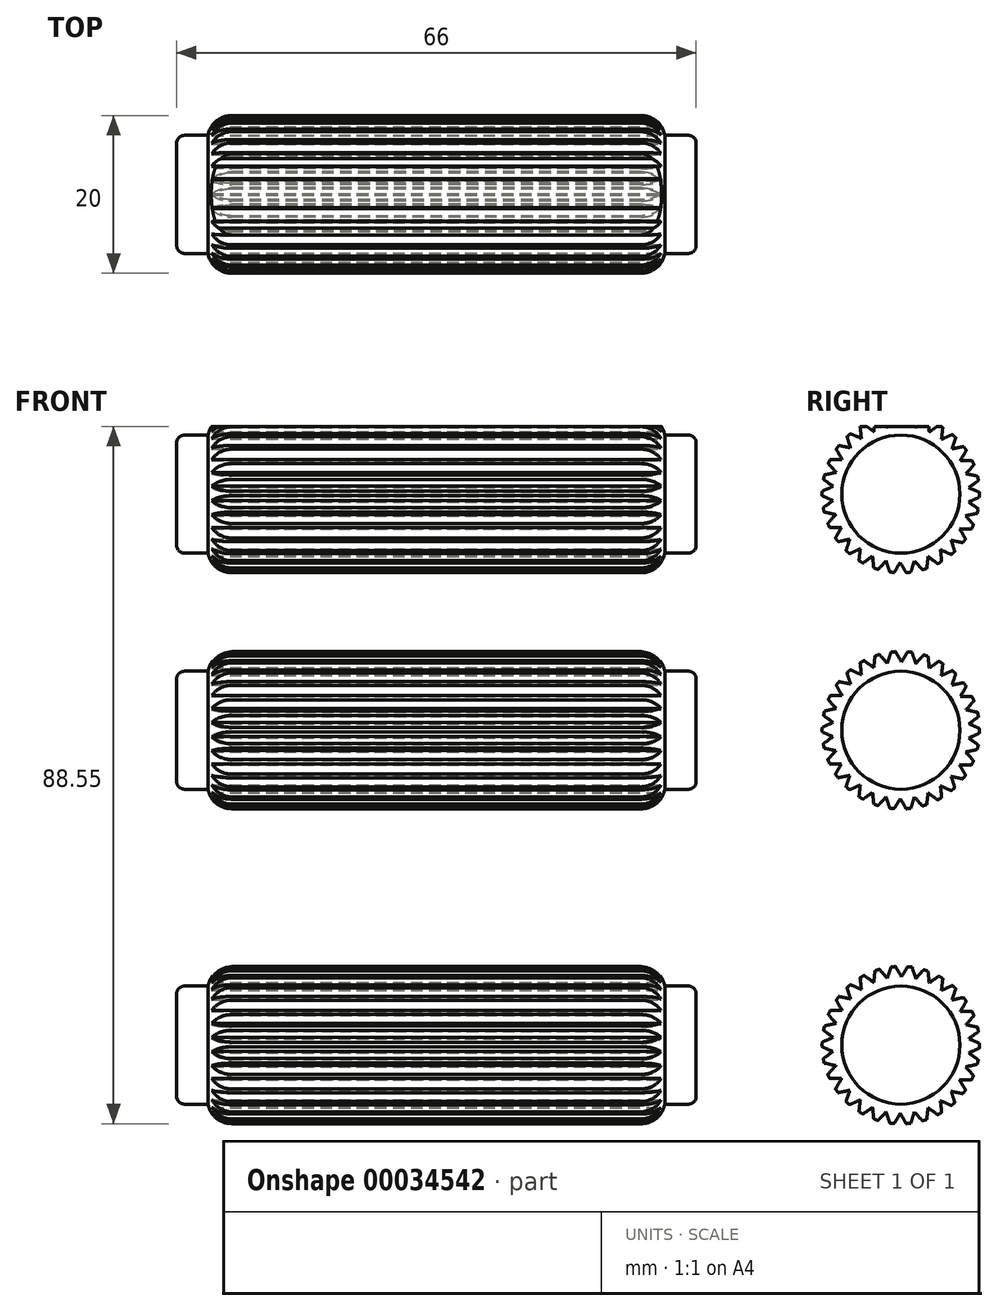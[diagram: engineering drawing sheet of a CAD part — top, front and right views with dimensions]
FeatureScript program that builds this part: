
annotation { "Feature Type Name" : "Feature", "Feature Type Description" : "" }
export const myFeature = defineFeature(function(context is Context, id is Id, definition is map)
    precondition{}
    {
        {
            var Q0;
            Q0=qCreatedBy(makeId("Top.planeOp"),FACE);
            var sketch = newSketch(context, id + "F0", { "sketchPlane" : qUnion([Q0])});
            skLineSegment(sketch, "E0.bottom", {"start": v(-73.95, 30.98) * mm, "end": v(-15.95, 30.98) * mm});
            skLineSegment(sketch, "E0.top", {"start": v(-73.95, 20.98) * mm, "end": v(-15.95, 20.98) * mm});
            skLineSegment(sketch, "E0.left", {"start": v(-73.95, 30.98) * mm, "end": v(-73.95, 20.98) * mm});
            skLineSegment(sketch, "E0.right", {"start": v(-15.95, 30.98) * mm, "end": v(-15.95, 20.98) * mm});
            skLineSegment(sketch, "E1.bottom", {"start": v(-15.95, 20.98) * mm, "end": v(-11.95, 20.98) * mm});
            skLineSegment(sketch, "E1.top", {"start": v(-15.95, 28.48) * mm, "end": v(-11.95, 28.48) * mm});
            skLineSegment(sketch, "E1.left", {"start": v(-15.95, 20.98) * mm, "end": v(-15.95, 28.48) * mm});
            skLineSegment(sketch, "E1.right", {"start": v(-11.95, 20.98) * mm, "end": v(-11.95, 28.48) * mm});
            skLineSegment(sketch, "E2", {"start": v(-44.95, 6.9) * mm, "end": v(-44.95, 44.2) * mm});
            skPoint(sketch, "E2.startSnap0", {"position": v(-44.95, 20.98) * mm});
            skLineSegment(sketch, "E3.MirrorCS", {"start": v(-73.95, 20.98) * mm, "end": v(-77.95, 20.98) * mm});
            skLineSegment(sketch, "E4.MirrorCS", {"start": v(-73.95, 20.98) * mm, "end": v(-73.95, 28.48) * mm});
            skLineSegment(sketch, "E5.MirrorCS", {"start": v(-77.95, 20.98) * mm, "end": v(-77.95, 28.48) * mm});
            skLineSegment(sketch, "E6.MirrorCS", {"start": v(-73.95, 28.48) * mm, "end": v(-77.95, 28.48) * mm});
            skSolve(sketch);
        }
        {
            var Q0;
            Q0=makeQuery(id+"F0.imprint","IMPRINT",FACE,{"disambiguationData":[TD([[makeQuery(id+"F0.imprint","IMPRINT",EDGE,{"derivedFrom":sQuery(id+"F0.wireOp",EDGE,"E3.MirrorCS")}),-1.0]])]});
            var Q1;
            {var subQ6=sQuery(id+"F0.wireOp",EDGE,"E0.left");Q1=makeQuery(id+"F0.imprint","IMPRINT",FACE,{"disambiguationData":[TD([[makeQuery(id+"F0.imprint","IMPRINT",EDGE,{"derivedFrom":subQ6}),1.0]])]});}
            var Q2;
            {var subQ6=sQuery(id+"F0.wireOp",EDGE,"E0.right");Q2=makeQuery(id+"F0.imprint","IMPRINT",FACE,{"disambiguationData":[TD([[makeQuery(id+"F0.imprint","IMPRINT",EDGE,{"derivedFrom":subQ6}),-1.0]])]});}
            var Q3;
            Q3=makeQuery(id+"F0.imprint","IMPRINT",FACE,{"disambiguationData":[TD([[makeQuery(id+"F0.imprint","IMPRINT",EDGE,{"derivedFrom":sQuery(id+"F0.wireOp",EDGE,"E1.bottom")}),1.0]])]});
            var Q4;
            Q4=sQuery(id+"F0.wireOp",EDGE,"E0.top");
            revolve(context, id + "F1", {"entities" : qUnion([Q0, Q1, Q2, Q3]), "axis" : qUnion([Q4]), "revolveType" : RevolveType.FULL});
        }
        {
            var Q0;
            Q0=qCreatedBy(makeId("Right.planeOp"),FACE);
            var sketch = newSketch(context, id + "F2", { "sketchPlane" : qUnion([Q0])});
            skCircle(sketch, "E7.0.0", {"center": v(20.98, 0) * mm, "radius": 7.5 * mm});
            skCircle(sketch, "E8.cCircle", {"center": v(21.07, 10) * mm, "radius": 0.66 * mm, "construction": true});
            skLineSegment(sketch, "E8.0", {"start": v(22.22, 10.65) * mm, "end": v(21.07, 8.67) * mm});
            skLineSegment(sketch, "E8.1", {"start": v(21.07, 8.67) * mm, "end": v(19.92, 10.65) * mm});
            skLineSegment(sketch, "E8.2", {"start": v(19.92, 10.65) * mm, "end": v(22.22, 10.65) * mm});
            skPoint(sketch, "E8.0.midPoint", {"position": v(21.64, 9.66) * mm});
            skLineSegment(sketch, "E9.1.0", {"start": v(19.27, 8.5) * mm, "end": v(17.73, 10.2) * mm});
            skLineSegment(sketch, "E9.1.1", {"start": v(19.98, 10.68) * mm, "end": v(19.27, 8.5) * mm});
            skLineSegment(sketch, "E9.1.2", {"start": v(17.73, 10.2) * mm, "end": v(19.98, 10.68) * mm});
            skLineSegment(sketch, "E9.2.0", {"start": v(17.54, 7.95) * mm, "end": v(15.68, 9.3) * mm});
            skLineSegment(sketch, "E9.2.1", {"start": v(17.78, 10.24) * mm, "end": v(17.54, 7.95) * mm});
            skLineSegment(sketch, "E9.2.2", {"start": v(15.68, 9.3) * mm, "end": v(17.78, 10.24) * mm});
            skLineSegment(sketch, "E10.1.3.0", {"start": v(15.96, 7.06) * mm, "end": v(13.86, 8) * mm});
            skLineSegment(sketch, "E10.3.3.0", {"start": v(15.72, 9.35) * mm, "end": v(15.96, 7.06) * mm});
            skLineSegment(sketch, "E10.6.3.0", {"start": v(13.86, 8) * mm, "end": v(15.72, 9.35) * mm});
            skLineSegment(sketch, "E10.1.4.0", {"start": v(14.6, 5.86) * mm, "end": v(12.35, 6.34) * mm});
            skLineSegment(sketch, "E10.3.4.0", {"start": v(13.9, 8.05) * mm, "end": v(14.6, 5.86) * mm});
            skLineSegment(sketch, "E10.6.4.0", {"start": v(12.35, 6.34) * mm, "end": v(13.9, 8.05) * mm});
            skLineSegment(sketch, "E10.1.5.0", {"start": v(13.52, 4.4) * mm, "end": v(11.23, 4.4) * mm});
            skLineSegment(sketch, "E10.3.5.0", {"start": v(12.37, 6.4) * mm, "end": v(13.52, 4.4) * mm});
            skLineSegment(sketch, "E10.6.5.0", {"start": v(11.23, 4.4) * mm, "end": v(12.37, 6.4) * mm});
            skLineSegment(sketch, "E10.1.6.0", {"start": v(12.77, 2.76) * mm, "end": v(10.52, 2.28) * mm});
            skLineSegment(sketch, "E10.3.6.0", {"start": v(11.23, 4.47) * mm, "end": v(12.77, 2.76) * mm});
            skLineSegment(sketch, "E10.6.6.0", {"start": v(10.52, 2.28) * mm, "end": v(11.23, 4.47) * mm});
            skLineSegment(sketch, "E10.1.7.0", {"start": v(12.37, 1) * mm, "end": v(10.28, 0.06) * mm});
            skLineSegment(sketch, "E10.3.7.0", {"start": v(10.52, 2.34) * mm, "end": v(12.37, 1) * mm});
            skLineSegment(sketch, "E10.6.7.0", {"start": v(10.28, 0.06) * mm, "end": v(10.52, 2.34) * mm});
            skLineSegment(sketch, "E10.1.8.0", {"start": v(12.36, -0.82) * mm, "end": v(10.5, -2.17) * mm});
            skLineSegment(sketch, "E10.3.8.0", {"start": v(10.26, 0.11) * mm, "end": v(12.36, -0.82) * mm});
            skLineSegment(sketch, "E10.6.8.0", {"start": v(10.5, -2.17) * mm, "end": v(10.26, 0.11) * mm});
            skLineSegment(sketch, "E10.1.9.0", {"start": v(12.71, -2.6) * mm, "end": v(11.18, -4.3) * mm});
            skLineSegment(sketch, "E10.3.9.0", {"start": v(10.47, -2.12) * mm, "end": v(12.71, -2.6) * mm});
            skLineSegment(sketch, "E10.6.9.0", {"start": v(11.18, -4.3) * mm, "end": v(10.47, -2.12) * mm});
            skLineSegment(sketch, "E10.1.10.0", {"start": v(13.43, -4.26) * mm, "end": v(12.29, -6.25) * mm});
            skLineSegment(sketch, "E10.3.10.0", {"start": v(11.14, -4.26) * mm, "end": v(13.43, -4.26) * mm});
            skLineSegment(sketch, "E10.6.10.0", {"start": v(12.29, -6.25) * mm, "end": v(11.14, -4.26) * mm});
            skLineSegment(sketch, "E10.1.11.0", {"start": v(14.48, -5.73) * mm, "end": v(13.78, -7.92) * mm});
            skLineSegment(sketch, "E10.3.11.0", {"start": v(12.24, -6.21) * mm, "end": v(14.48, -5.73) * mm});
            skLineSegment(sketch, "E10.6.11.0", {"start": v(13.78, -7.92) * mm, "end": v(12.24, -6.21) * mm});
            skLineSegment(sketch, "E10.1.12.0", {"start": v(15.82, -6.96) * mm, "end": v(15.58, -9.24) * mm});
            skLineSegment(sketch, "E10.3.12.0", {"start": v(13.72, -7.9) * mm, "end": v(15.82, -6.96) * mm});
            skLineSegment(sketch, "E10.6.12.0", {"start": v(15.58, -9.24) * mm, "end": v(13.72, -7.9) * mm});
            skLineSegment(sketch, "E10.1.13.0", {"start": v(17.38, -7.88) * mm, "end": v(17.62, -10.16) * mm});
            skLineSegment(sketch, "E10.3.13.0", {"start": v(15.52, -9.23) * mm, "end": v(17.38, -7.88) * mm});
            skLineSegment(sketch, "E10.6.13.0", {"start": v(17.62, -10.16) * mm, "end": v(15.52, -9.23) * mm});
            skLineSegment(sketch, "E10.1.14.0", {"start": v(19.1, -8.46) * mm, "end": v(19.8, -10.64) * mm});
            skLineSegment(sketch, "E10.3.14.0", {"start": v(17.56, -10.16) * mm, "end": v(19.1, -8.46) * mm});
            skLineSegment(sketch, "E10.6.14.0", {"start": v(19.8, -10.64) * mm, "end": v(17.56, -10.16) * mm});
            skLineSegment(sketch, "E10.1.15.0", {"start": v(20.9, -8.67) * mm, "end": v(22.04, -10.65) * mm});
            skLineSegment(sketch, "E10.3.15.0", {"start": v(19.75, -10.65) * mm, "end": v(20.9, -8.67) * mm});
            skLineSegment(sketch, "E10.6.15.0", {"start": v(22.04, -10.65) * mm, "end": v(19.75, -10.65) * mm});
            skLineSegment(sketch, "E10.1.16.0", {"start": v(22.7, -8.5) * mm, "end": v(24.24, -10.2) * mm});
            skLineSegment(sketch, "E10.3.16.0", {"start": v(22, -10.68) * mm, "end": v(22.7, -8.5) * mm});
            skLineSegment(sketch, "E10.6.16.0", {"start": v(24.24, -10.2) * mm, "end": v(22, -10.68) * mm});
            skLineSegment(sketch, "E10.1.17.0", {"start": v(24.43, -7.95) * mm, "end": v(26.29, -9.3) * mm});
            skLineSegment(sketch, "E10.3.17.0", {"start": v(24.19, -10.24) * mm, "end": v(24.43, -7.95) * mm});
            skLineSegment(sketch, "E10.6.17.0", {"start": v(26.29, -9.3) * mm, "end": v(24.19, -10.24) * mm});
            skLineSegment(sketch, "E10.1.18.0", {"start": v(26, -7.06) * mm, "end": v(28.1, -8) * mm});
            skLineSegment(sketch, "E10.3.18.0", {"start": v(26.25, -9.35) * mm, "end": v(26, -7.06) * mm});
            skLineSegment(sketch, "E10.6.18.0", {"start": v(28.1, -8) * mm, "end": v(26.25, -9.35) * mm});
            skLineSegment(sketch, "E10.1.19.0", {"start": v(27.36, -5.86) * mm, "end": v(29.61, -6.34) * mm});
            skLineSegment(sketch, "E10.3.19.0", {"start": v(28.07, -8.05) * mm, "end": v(27.36, -5.86) * mm});
            skLineSegment(sketch, "E10.6.19.0", {"start": v(29.61, -6.34) * mm, "end": v(28.07, -8.05) * mm});
            skLineSegment(sketch, "E11.1.20.0", {"start": v(28.44, -4.4) * mm, "end": v(30.74, -4.4) * mm});
            skLineSegment(sketch, "E11.3.20.0", {"start": v(29.6, -6.4) * mm, "end": v(28.44, -4.4) * mm});
            skLineSegment(sketch, "E11.6.20.0", {"start": v(30.74, -4.4) * mm, "end": v(29.6, -6.4) * mm});
            skLineSegment(sketch, "E11.1.21.0", {"start": v(29.2, -2.76) * mm, "end": v(31.44, -2.28) * mm});
            skLineSegment(sketch, "E11.3.21.0", {"start": v(30.73, -4.47) * mm, "end": v(29.2, -2.76) * mm});
            skLineSegment(sketch, "E11.6.21.0", {"start": v(31.44, -2.28) * mm, "end": v(30.73, -4.47) * mm});
            skLineSegment(sketch, "E11.1.22.0", {"start": v(29.6, -1) * mm, "end": v(31.69, -0.06) * mm});
            skLineSegment(sketch, "E11.3.22.0", {"start": v(31.45, -2.34) * mm, "end": v(29.6, -1) * mm});
            skLineSegment(sketch, "E11.6.22.0", {"start": v(31.69, -0.06) * mm, "end": v(31.45, -2.34) * mm});
            skLineSegment(sketch, "E11.1.23.0", {"start": v(29.61, 0.82) * mm, "end": v(31.47, 2.17) * mm});
            skLineSegment(sketch, "E11.3.23.0", {"start": v(31.7, -0.11) * mm, "end": v(29.61, 0.82) * mm});
            skLineSegment(sketch, "E11.6.23.0", {"start": v(31.47, 2.17) * mm, "end": v(31.7, -0.11) * mm});
            skLineSegment(sketch, "E11.1.24.0", {"start": v(29.25, 2.6) * mm, "end": v(30.79, 4.3) * mm});
            skLineSegment(sketch, "E11.3.24.0", {"start": v(31.5, 2.12) * mm, "end": v(29.25, 2.6) * mm});
            skLineSegment(sketch, "E11.6.24.0", {"start": v(30.79, 4.3) * mm, "end": v(31.5, 2.12) * mm});
            skLineSegment(sketch, "E11.1.25.0", {"start": v(28.53, 4.26) * mm, "end": v(29.68, 6.25) * mm});
            skLineSegment(sketch, "E11.3.25.0", {"start": v(30.83, 4.26) * mm, "end": v(28.53, 4.26) * mm});
            skLineSegment(sketch, "E11.6.25.0", {"start": v(29.68, 6.25) * mm, "end": v(30.83, 4.26) * mm});
            skLineSegment(sketch, "E11.1.26.0", {"start": v(27.48, 5.73) * mm, "end": v(28.2, 7.92) * mm});
            skLineSegment(sketch, "E11.3.26.0", {"start": v(29.73, 6.21) * mm, "end": v(27.48, 5.73) * mm});
            skLineSegment(sketch, "E11.6.26.0", {"start": v(28.2, 7.92) * mm, "end": v(29.73, 6.21) * mm});
            skLineSegment(sketch, "E11.1.27.0", {"start": v(26.15, 6.96) * mm, "end": v(26.39, 9.24) * mm});
            skLineSegment(sketch, "E11.3.27.0", {"start": v(28.24, 7.9) * mm, "end": v(26.15, 6.96) * mm});
            skLineSegment(sketch, "E11.6.27.0", {"start": v(26.39, 9.24) * mm, "end": v(28.24, 7.9) * mm});
            skLineSegment(sketch, "E11.1.28.0", {"start": v(24.59, 7.88) * mm, "end": v(24.35, 10.16) * mm});
            skLineSegment(sketch, "E11.3.28.0", {"start": v(26.44, 9.23) * mm, "end": v(24.59, 7.88) * mm});
            skLineSegment(sketch, "E11.6.28.0", {"start": v(24.35, 10.16) * mm, "end": v(26.44, 9.23) * mm});
            skLineSegment(sketch, "E11.1.29.0", {"start": v(22.87, 8.46) * mm, "end": v(22.16, 10.64) * mm});
            skLineSegment(sketch, "E11.3.29.0", {"start": v(24.4, 10.16) * mm, "end": v(22.87, 8.46) * mm});
            skLineSegment(sketch, "E11.6.29.0", {"start": v(22.16, 10.64) * mm, "end": v(24.4, 10.16) * mm});
            skSolve(sketch);
        }
        {
            var Q0;
            {var subQ0=sQuery(id+"F0.wireOp",EDGE,"E0.bottom");var subQ1=sQuery(id+"F0.wireOp",EDGE,"E0.right");var subQ3=sQuery(id+"F2.wireOp",EDGE,"E9.2.0");Q0=makeQuery(id+"F5.boolean.opBoolean","SPLIT",EDGE,{"disambiguationData":[TD([makeQuery(id+"F5.opExtrude","SWEPT_FACE",FACE,{"disambiguationData":[OSD([subQ3]),TDD([makeQuery(id+"F2.imprint","IMPRINT",EDGE,{"disambiguationData":[TD([[makeQuery(id+"F2.imprint","INTERSECT",VERTEX,{"derivedFrom":[subQ3,sQuery(id+"F2.wireOp",EDGE,"E9.2.1")]}),-1.0]])],"derivedFrom":subQ3})])]})])],"derivedFrom":makeQuery(id+"F1.opRevolve","SWEPT_EDGE",EDGE,{"disambiguationData":[OSD([subQ0,subQ1])]})});}
            var Q1;
            {var subQ0=sQuery(id+"F0.wireOp",EDGE,"E0.bottom");var subQ1=sQuery(id+"F0.wireOp",EDGE,"E0.right");var subQ3=sQuery(id+"F2.wireOp",EDGE,"E10.1.3.0");Q1=makeQuery(id+"F5.boolean.opBoolean","SPLIT",EDGE,{"disambiguationData":[TD([makeQuery(id+"F5.opExtrude","SWEPT_FACE",FACE,{"disambiguationData":[OSD([subQ3]),TDD([makeQuery(id+"F2.imprint","IMPRINT",EDGE,{"disambiguationData":[TD([[makeQuery(id+"F2.imprint","INTERSECT",VERTEX,{"derivedFrom":[subQ3,sQuery(id+"F2.wireOp",EDGE,"E10.3.3.0")]}),-1.0]])],"derivedFrom":subQ3})])]})])],"derivedFrom":makeQuery(id+"F1.opRevolve","SWEPT_EDGE",EDGE,{"disambiguationData":[OSD([subQ0,subQ1])]})});}
            fillet(context, id + "F3", {"entities" : qUnion([Q0, Q1]), "radius" : 3 * mm, "tangentPropagation" : true, "allowEdgeOverflow" : false});
        }
        {
            var Q0;
            Q0=makeQuery(id+"F1.opRevolve","SWEPT_EDGE",EDGE,{"disambiguationData":[OSD([sQuery(id+"F0.wireOp",EDGE,"E0.bottom"),sQuery(id+"F0.wireOp",EDGE,"E0.left")])]});
            fillet(context, id + "F4", {"entities" : qUnion([Q0]), "radius" : 3 * mm, "tangentPropagation" : true, "allowEdgeOverflow" : false});
        }
        {
            var Q0;
            {var subQ7=sQuery(id+"F2.wireOp",EDGE,"E9.1.0");var subQ10=sQuery(id+"F2.wireOp",EDGE,"E9.1.2");var subQ12=makeQuery(id+"F2.imprint","INTERSECT",VERTEX,{"derivedFrom":[subQ7,subQ10]});Q0=makeQuery(id+"F2.imprint","IMPRINT",FACE,{"disambiguationData":[TD([[makeQuery(id+"F2.imprint","IMPRINT",EDGE,{"disambiguationData":[TD([[subQ12,1.0]])],"derivedFrom":subQ7}),1.0]])]});}
            var Q1;
            {var subQ7=sQuery(id+"F2.wireOp",EDGE,"E8.1");var subQ10=sQuery(id+"F2.wireOp",EDGE,"E8.2");var subQ12=makeQuery(id+"F2.imprint","INTERSECT",VERTEX,{"derivedFrom":[subQ7,subQ10]});Q1=makeQuery(id+"F2.imprint","IMPRINT",FACE,{"disambiguationData":[TD([[makeQuery(id+"F2.imprint","IMPRINT",EDGE,{"disambiguationData":[TD([[subQ12,1.0]])],"derivedFrom":subQ7}),1.0]])]});}
            var Q2;
            {var subQ7=sQuery(id+"F2.wireOp",EDGE,"E9.2.0");var subQ10=sQuery(id+"F2.wireOp",EDGE,"E9.2.2");var subQ12=makeQuery(id+"F2.imprint","INTERSECT",VERTEX,{"derivedFrom":[subQ7,subQ10]});Q2=makeQuery(id+"F2.imprint","IMPRINT",FACE,{"disambiguationData":[TD([[makeQuery(id+"F2.imprint","IMPRINT",EDGE,{"disambiguationData":[TD([[subQ12,1.0]])],"derivedFrom":subQ7}),1.0]])]});}
            var Q3;
            {var subQ7=sQuery(id+"F2.wireOp",EDGE,"E10.1.3.0");var subQ10=sQuery(id+"F2.wireOp",EDGE,"E10.6.3.0");var subQ12=makeQuery(id+"F2.imprint","INTERSECT",VERTEX,{"derivedFrom":[subQ7,subQ10]});Q3=makeQuery(id+"F2.imprint","IMPRINT",FACE,{"disambiguationData":[TD([[makeQuery(id+"F2.imprint","IMPRINT",EDGE,{"disambiguationData":[TD([[subQ12,1.0]])],"derivedFrom":subQ7}),1.0]])]});}
            var Q4;
            {var subQ7=sQuery(id+"F2.wireOp",EDGE,"E10.1.4.0");var subQ10=sQuery(id+"F2.wireOp",EDGE,"E10.6.4.0");var subQ12=makeQuery(id+"F2.imprint","INTERSECT",VERTEX,{"derivedFrom":[subQ7,subQ10]});Q4=makeQuery(id+"F2.imprint","IMPRINT",FACE,{"disambiguationData":[TD([[makeQuery(id+"F2.imprint","IMPRINT",EDGE,{"disambiguationData":[TD([[subQ12,1.0]])],"derivedFrom":subQ7}),1.0]])]});}
            var Q5;
            {var subQ7=sQuery(id+"F2.wireOp",EDGE,"E10.1.5.0");var subQ10=sQuery(id+"F2.wireOp",EDGE,"E10.6.5.0");var subQ12=makeQuery(id+"F2.imprint","INTERSECT",VERTEX,{"derivedFrom":[subQ7,subQ10]});Q5=makeQuery(id+"F2.imprint","IMPRINT",FACE,{"disambiguationData":[TD([[makeQuery(id+"F2.imprint","IMPRINT",EDGE,{"disambiguationData":[TD([[subQ12,1.0]])],"derivedFrom":subQ7}),1.0]])]});}
            var Q6;
            {var subQ7=sQuery(id+"F2.wireOp",EDGE,"E10.1.6.0");var subQ10=sQuery(id+"F2.wireOp",EDGE,"E10.6.6.0");var subQ12=makeQuery(id+"F2.imprint","INTERSECT",VERTEX,{"derivedFrom":[subQ7,subQ10]});Q6=makeQuery(id+"F2.imprint","IMPRINT",FACE,{"disambiguationData":[TD([[makeQuery(id+"F2.imprint","IMPRINT",EDGE,{"disambiguationData":[TD([[subQ12,1.0]])],"derivedFrom":subQ7}),1.0]])]});}
            var Q7;
            {var subQ7=sQuery(id+"F2.wireOp",EDGE,"E10.1.8.0");var subQ10=sQuery(id+"F2.wireOp",EDGE,"E10.6.8.0");var subQ12=makeQuery(id+"F2.imprint","INTERSECT",VERTEX,{"derivedFrom":[subQ7,subQ10]});Q7=makeQuery(id+"F2.imprint","IMPRINT",FACE,{"disambiguationData":[TD([[makeQuery(id+"F2.imprint","IMPRINT",EDGE,{"disambiguationData":[TD([[subQ12,1.0]])],"derivedFrom":subQ7}),1.0]])]});}
            var Q8;
            {var subQ7=sQuery(id+"F2.wireOp",EDGE,"E10.1.7.0");var subQ10=sQuery(id+"F2.wireOp",EDGE,"E10.6.7.0");var subQ12=makeQuery(id+"F2.imprint","INTERSECT",VERTEX,{"derivedFrom":[subQ7,subQ10]});Q8=makeQuery(id+"F2.imprint","IMPRINT",FACE,{"disambiguationData":[TD([[makeQuery(id+"F2.imprint","IMPRINT",EDGE,{"disambiguationData":[TD([[subQ12,1.0]])],"derivedFrom":subQ7}),1.0]])]});}
            var Q9;
            {var subQ7=sQuery(id+"F2.wireOp",EDGE,"E10.1.9.0");var subQ10=sQuery(id+"F2.wireOp",EDGE,"E10.6.9.0");var subQ12=makeQuery(id+"F2.imprint","INTERSECT",VERTEX,{"derivedFrom":[subQ7,subQ10]});Q9=makeQuery(id+"F2.imprint","IMPRINT",FACE,{"disambiguationData":[TD([[makeQuery(id+"F2.imprint","IMPRINT",EDGE,{"disambiguationData":[TD([[subQ12,1.0]])],"derivedFrom":subQ7}),1.0]])]});}
            var Q10;
            {var subQ7=sQuery(id+"F2.wireOp",EDGE,"E10.1.10.0");var subQ10=sQuery(id+"F2.wireOp",EDGE,"E10.6.10.0");var subQ12=makeQuery(id+"F2.imprint","INTERSECT",VERTEX,{"derivedFrom":[subQ7,subQ10]});Q10=makeQuery(id+"F2.imprint","IMPRINT",FACE,{"disambiguationData":[TD([[makeQuery(id+"F2.imprint","IMPRINT",EDGE,{"disambiguationData":[TD([[subQ12,1.0]])],"derivedFrom":subQ7}),1.0]])]});}
            var Q11;
            {var subQ7=sQuery(id+"F2.wireOp",EDGE,"E10.1.11.0");var subQ10=sQuery(id+"F2.wireOp",EDGE,"E10.6.11.0");var subQ12=makeQuery(id+"F2.imprint","INTERSECT",VERTEX,{"derivedFrom":[subQ7,subQ10]});Q11=makeQuery(id+"F2.imprint","IMPRINT",FACE,{"disambiguationData":[TD([[makeQuery(id+"F2.imprint","IMPRINT",EDGE,{"disambiguationData":[TD([[subQ12,1.0]])],"derivedFrom":subQ7}),1.0]])]});}
            var Q12;
            {var subQ7=sQuery(id+"F2.wireOp",EDGE,"E10.1.13.0");var subQ10=sQuery(id+"F2.wireOp",EDGE,"E10.6.13.0");var subQ12=makeQuery(id+"F2.imprint","INTERSECT",VERTEX,{"derivedFrom":[subQ7,subQ10]});Q12=makeQuery(id+"F2.imprint","IMPRINT",FACE,{"disambiguationData":[TD([[makeQuery(id+"F2.imprint","IMPRINT",EDGE,{"disambiguationData":[TD([[subQ12,1.0]])],"derivedFrom":subQ7}),1.0]])]});}
            var Q13;
            {var subQ7=sQuery(id+"F2.wireOp",EDGE,"E10.1.14.0");var subQ10=sQuery(id+"F2.wireOp",EDGE,"E10.6.14.0");var subQ12=makeQuery(id+"F2.imprint","INTERSECT",VERTEX,{"derivedFrom":[subQ7,subQ10]});Q13=makeQuery(id+"F2.imprint","IMPRINT",FACE,{"disambiguationData":[TD([[makeQuery(id+"F2.imprint","IMPRINT",EDGE,{"disambiguationData":[TD([[subQ12,1.0]])],"derivedFrom":subQ7}),1.0]])]});}
            var Q14;
            {var subQ7=sQuery(id+"F2.wireOp",EDGE,"E10.1.15.0");var subQ10=sQuery(id+"F2.wireOp",EDGE,"E10.6.15.0");var subQ12=makeQuery(id+"F2.imprint","INTERSECT",VERTEX,{"derivedFrom":[subQ7,subQ10]});Q14=makeQuery(id+"F2.imprint","IMPRINT",FACE,{"disambiguationData":[TD([[makeQuery(id+"F2.imprint","IMPRINT",EDGE,{"disambiguationData":[TD([[subQ12,1.0]])],"derivedFrom":subQ7}),1.0]])]});}
            var Q15;
            {var subQ7=sQuery(id+"F2.wireOp",EDGE,"E10.1.16.0");var subQ10=sQuery(id+"F2.wireOp",EDGE,"E10.6.16.0");var subQ12=makeQuery(id+"F2.imprint","INTERSECT",VERTEX,{"derivedFrom":[subQ7,subQ10]});Q15=makeQuery(id+"F2.imprint","IMPRINT",FACE,{"disambiguationData":[TD([[makeQuery(id+"F2.imprint","IMPRINT",EDGE,{"disambiguationData":[TD([[subQ12,1.0]])],"derivedFrom":subQ7}),1.0]])]});}
            var Q16;
            {var subQ7=sQuery(id+"F2.wireOp",EDGE,"E10.1.17.0");var subQ10=sQuery(id+"F2.wireOp",EDGE,"E10.6.17.0");var subQ12=makeQuery(id+"F2.imprint","INTERSECT",VERTEX,{"derivedFrom":[subQ7,subQ10]});Q16=makeQuery(id+"F2.imprint","IMPRINT",FACE,{"disambiguationData":[TD([[makeQuery(id+"F2.imprint","IMPRINT",EDGE,{"disambiguationData":[TD([[subQ12,1.0]])],"derivedFrom":subQ7}),1.0]])]});}
            var Q17;
            {var subQ7=sQuery(id+"F2.wireOp",EDGE,"E10.1.18.0");var subQ10=sQuery(id+"F2.wireOp",EDGE,"E10.6.18.0");var subQ12=makeQuery(id+"F2.imprint","INTERSECT",VERTEX,{"derivedFrom":[subQ7,subQ10]});Q17=makeQuery(id+"F2.imprint","IMPRINT",FACE,{"disambiguationData":[TD([[makeQuery(id+"F2.imprint","IMPRINT",EDGE,{"disambiguationData":[TD([[subQ12,1.0]])],"derivedFrom":subQ7}),1.0]])]});}
            var Q18;
            {var subQ7=sQuery(id+"F2.wireOp",EDGE,"E10.1.19.0");var subQ10=sQuery(id+"F2.wireOp",EDGE,"E10.6.19.0");var subQ12=makeQuery(id+"F2.imprint","INTERSECT",VERTEX,{"derivedFrom":[subQ7,subQ10]});Q18=makeQuery(id+"F2.imprint","IMPRINT",FACE,{"disambiguationData":[TD([[makeQuery(id+"F2.imprint","IMPRINT",EDGE,{"disambiguationData":[TD([[subQ12,1.0]])],"derivedFrom":subQ7}),1.0]])]});}
            var Q19;
            {var subQ7=sQuery(id+"F2.wireOp",EDGE,"E11.1.20.0");var subQ10=sQuery(id+"F2.wireOp",EDGE,"E11.6.20.0");var subQ12=makeQuery(id+"F2.imprint","INTERSECT",VERTEX,{"derivedFrom":[subQ7,subQ10]});Q19=makeQuery(id+"F2.imprint","IMPRINT",FACE,{"disambiguationData":[TD([[makeQuery(id+"F2.imprint","IMPRINT",EDGE,{"disambiguationData":[TD([[subQ12,1.0]])],"derivedFrom":subQ7}),1.0]])]});}
            var Q20;
            {var subQ7=sQuery(id+"F2.wireOp",EDGE,"E11.1.21.0");var subQ10=sQuery(id+"F2.wireOp",EDGE,"E11.6.21.0");var subQ12=makeQuery(id+"F2.imprint","INTERSECT",VERTEX,{"derivedFrom":[subQ7,subQ10]});Q20=makeQuery(id+"F2.imprint","IMPRINT",FACE,{"disambiguationData":[TD([[makeQuery(id+"F2.imprint","IMPRINT",EDGE,{"disambiguationData":[TD([[subQ12,1.0]])],"derivedFrom":subQ7}),1.0]])]});}
            var Q21;
            {var subQ7=sQuery(id+"F2.wireOp",EDGE,"E11.1.22.0");var subQ10=sQuery(id+"F2.wireOp",EDGE,"E11.6.22.0");var subQ12=makeQuery(id+"F2.imprint","INTERSECT",VERTEX,{"derivedFrom":[subQ7,subQ10]});Q21=makeQuery(id+"F2.imprint","IMPRINT",FACE,{"disambiguationData":[TD([[makeQuery(id+"F2.imprint","IMPRINT",EDGE,{"disambiguationData":[TD([[subQ12,1.0]])],"derivedFrom":subQ7}),1.0]])]});}
            var Q22;
            {var subQ7=sQuery(id+"F2.wireOp",EDGE,"E11.1.23.0");var subQ10=sQuery(id+"F2.wireOp",EDGE,"E11.6.23.0");var subQ12=makeQuery(id+"F2.imprint","INTERSECT",VERTEX,{"derivedFrom":[subQ7,subQ10]});Q22=makeQuery(id+"F2.imprint","IMPRINT",FACE,{"disambiguationData":[TD([[makeQuery(id+"F2.imprint","IMPRINT",EDGE,{"disambiguationData":[TD([[subQ12,1.0]])],"derivedFrom":subQ7}),1.0]])]});}
            var Q23;
            {var subQ7=sQuery(id+"F2.wireOp",EDGE,"E11.1.24.0");var subQ10=sQuery(id+"F2.wireOp",EDGE,"E11.6.24.0");var subQ12=makeQuery(id+"F2.imprint","INTERSECT",VERTEX,{"derivedFrom":[subQ7,subQ10]});Q23=makeQuery(id+"F2.imprint","IMPRINT",FACE,{"disambiguationData":[TD([[makeQuery(id+"F2.imprint","IMPRINT",EDGE,{"disambiguationData":[TD([[subQ12,1.0]])],"derivedFrom":subQ7}),1.0]])]});}
            var Q24;
            {var subQ7=sQuery(id+"F2.wireOp",EDGE,"E11.1.25.0");var subQ10=sQuery(id+"F2.wireOp",EDGE,"E11.6.25.0");var subQ12=makeQuery(id+"F2.imprint","INTERSECT",VERTEX,{"derivedFrom":[subQ7,subQ10]});Q24=makeQuery(id+"F2.imprint","IMPRINT",FACE,{"disambiguationData":[TD([[makeQuery(id+"F2.imprint","IMPRINT",EDGE,{"disambiguationData":[TD([[subQ12,1.0]])],"derivedFrom":subQ7}),1.0]])]});}
            var Q25;
            {var subQ7=sQuery(id+"F2.wireOp",EDGE,"E11.1.26.0");var subQ10=sQuery(id+"F2.wireOp",EDGE,"E11.6.26.0");var subQ12=makeQuery(id+"F2.imprint","INTERSECT",VERTEX,{"derivedFrom":[subQ7,subQ10]});Q25=makeQuery(id+"F2.imprint","IMPRINT",FACE,{"disambiguationData":[TD([[makeQuery(id+"F2.imprint","IMPRINT",EDGE,{"disambiguationData":[TD([[subQ12,1.0]])],"derivedFrom":subQ7}),1.0]])]});}
            var Q26;
            {var subQ7=sQuery(id+"F2.wireOp",EDGE,"E11.1.27.0");var subQ10=sQuery(id+"F2.wireOp",EDGE,"E11.6.27.0");var subQ12=makeQuery(id+"F2.imprint","INTERSECT",VERTEX,{"derivedFrom":[subQ7,subQ10]});Q26=makeQuery(id+"F2.imprint","IMPRINT",FACE,{"disambiguationData":[TD([[makeQuery(id+"F2.imprint","IMPRINT",EDGE,{"disambiguationData":[TD([[subQ12,1.0]])],"derivedFrom":subQ7}),1.0]])]});}
            var Q27;
            {var subQ0=sQuery(id+"F2.wireOp",EDGE,"E11.6.29.0");var subQ1=sQuery(id+"F2.wireOp",EDGE,"E8.0");var subQ2=makeQuery(id+"F2.imprint","INTERSECT",VERTEX,{"derivedFrom":[subQ1,subQ0]});Q27=makeQuery(id+"F2.imprint","IMPRINT",FACE,{"disambiguationData":[TD([[makeQuery(id+"F2.imprint","IMPRINT",EDGE,{"disambiguationData":[TD([[subQ2,-1.0]])],"derivedFrom":subQ1}),1.0]])]});}
            var Q28;
            {var subQ1=sQuery(id+"F2.wireOp",EDGE,"E8.0");var subQ8=sQuery(id+"F2.wireOp",EDGE,"E8.2");var subQ10=makeQuery(id+"F2.imprint","INTERSECT",VERTEX,{"derivedFrom":[subQ1,subQ8]});Q28=makeQuery(id+"F2.imprint","IMPRINT",FACE,{"disambiguationData":[TD([[makeQuery(id+"F2.imprint","IMPRINT",EDGE,{"disambiguationData":[TD([[subQ10,-1.0]])],"derivedFrom":subQ1}),-1.0]])]});}
            var Q29;
            {var subQ7=sQuery(id+"F2.wireOp",EDGE,"E10.1.12.0");var subQ10=sQuery(id+"F2.wireOp",EDGE,"E10.6.12.0");var subQ12=makeQuery(id+"F2.imprint","INTERSECT",VERTEX,{"derivedFrom":[subQ7,subQ10]});Q29=makeQuery(id+"F2.imprint","IMPRINT",FACE,{"disambiguationData":[TD([[makeQuery(id+"F2.imprint","IMPRINT",EDGE,{"disambiguationData":[TD([[subQ12,1.0]])],"derivedFrom":subQ7}),1.0]])]});}
            extrude(context, id + "F5", {"entities" : qUnion([Q0, Q1, Q2, Q3, Q4, Q5, Q6, Q7, Q8, Q9, Q10, Q11, Q12, Q13, Q14, Q15, Q16, Q17, Q18, Q19, Q20, Q21, Q22, Q23, Q24, Q25, Q26, Q27, Q28, Q29]), "operationType" : NewBodyOperationType.REMOVE, "endBound" : BoundingType.THROUGH_ALL, "oppositeDirection" : true, "depth" : 25 * mm});
        }
        {
            var Q0;
            Q0=makeQuery(id+"F1.opRevolve","SWEPT_EDGE",EDGE,{"disambiguationData":[OSD([sQuery(id+"F0.wireOp",EDGE,"E1.top"),sQuery(id+"F0.wireOp",EDGE,"E1.right")])]});
            fillet(context, id + "F6", {"entities" : qUnion([Q0]), "radius" : 1 * mm, "tangentPropagation" : true, "allowEdgeOverflow" : false});
        }
        {
            var Q0;
            Q0=makeQuery(id+"F1.opRevolve","SWEPT_EDGE",EDGE,{"disambiguationData":[OSD([sQuery(id+"F0.wireOp",EDGE,"E5.MirrorCS"),sQuery(id+"F0.wireOp",EDGE,"E6.MirrorCS")])]});
            fillet(context, id + "F7", {"entities" : qUnion([Q0]), "radius" : 1 * mm, "tangentPropagation" : true, "allowEdgeOverflow" : false});
        }
        {
            var Q0;
            Q0=makeQuery(id+"F1.opRevolve","SWEPT_BODY",BODY,{"disambiguationData":[OSD([sQuery(id+"F0.wireOp",EDGE,"E0.bottom"),sQuery(id+"F0.wireOp",EDGE,"E0.top"),sQuery(id+"F0.wireOp",EDGE,"E0.left"),sQuery(id+"F0.wireOp",EDGE,"E0.right"),sQuery(id+"F0.wireOp",EDGE,"E1.bottom"),sQuery(id+"F0.wireOp",EDGE,"E1.top"),sQuery(id+"F0.wireOp",EDGE,"E1.right"),sQuery(id+"F0.wireOp",EDGE,"E3.MirrorCS"),sQuery(id+"F0.wireOp",EDGE,"E5.MirrorCS"),sQuery(id+"F0.wireOp",EDGE,"E6.MirrorCS")])]});
            transform(context, id + "F8", {"entities" : qUnion([Q0]), "transformType" : TransformType.TRANSLATION_3D, "dx" : 0 * mm, "dy" : 30 * mm, "dz" : 0 * mm, "makeCopy" : true});
        }
        {
            var Q0;
            Q0=makeQuery(id+"F8.opPattern","COPY",BODY,{"derivedFrom":makeQuery(id+"F1.opRevolve","SWEPT_BODY",BODY,{"disambiguationData":[OSD([sQuery(id+"F0.wireOp",EDGE,"E0.bottom"),sQuery(id+"F0.wireOp",EDGE,"E0.top"),sQuery(id+"F0.wireOp",EDGE,"E0.left"),sQuery(id+"F0.wireOp",EDGE,"E0.right"),sQuery(id+"F0.wireOp",EDGE,"E1.bottom"),sQuery(id+"F0.wireOp",EDGE,"E1.top"),sQuery(id+"F0.wireOp",EDGE,"E1.right"),sQuery(id+"F0.wireOp",EDGE,"E3.MirrorCS"),sQuery(id+"F0.wireOp",EDGE,"E5.MirrorCS"),sQuery(id+"F0.wireOp",EDGE,"E6.MirrorCS")])]}),"instanceName":"1"});
            deleteBodies(context, id + "F9", {"entities" : qUnion([Q0])});
        }
        {
            var Q0;
            Q0=makeQuery(id+"F1.opRevolve","SWEPT_BODY",BODY,{"disambiguationData":[OSD([sQuery(id+"F0.wireOp",EDGE,"E0.bottom"),sQuery(id+"F0.wireOp",EDGE,"E0.top"),sQuery(id+"F0.wireOp",EDGE,"E0.left"),sQuery(id+"F0.wireOp",EDGE,"E0.right"),sQuery(id+"F0.wireOp",EDGE,"E1.bottom"),sQuery(id+"F0.wireOp",EDGE,"E1.top"),sQuery(id+"F0.wireOp",EDGE,"E1.right"),sQuery(id+"F0.wireOp",EDGE,"E3.MirrorCS"),sQuery(id+"F0.wireOp",EDGE,"E5.MirrorCS"),sQuery(id+"F0.wireOp",EDGE,"E6.MirrorCS")])]});
            transform(context, id + "F10", {"entities" : qUnion([Q0]), "transformType" : TransformType.TRANSLATION_3D, "dx" : 0 * mm, "dy" : 0 * mm, "dz" : 50 * mm, "makeCopy" : true});
        }
        {
            var Q0;
            Q0=makeQuery(id+"F10.opPattern","COPY",BODY,{"derivedFrom":makeQuery(id+"F1.opRevolve","SWEPT_BODY",BODY,{"disambiguationData":[OSD([sQuery(id+"F0.wireOp",EDGE,"E0.bottom"),sQuery(id+"F0.wireOp",EDGE,"E0.top"),sQuery(id+"F0.wireOp",EDGE,"E0.left"),sQuery(id+"F0.wireOp",EDGE,"E0.right"),sQuery(id+"F0.wireOp",EDGE,"E1.bottom"),sQuery(id+"F0.wireOp",EDGE,"E1.top"),sQuery(id+"F0.wireOp",EDGE,"E1.right"),sQuery(id+"F0.wireOp",EDGE,"E3.MirrorCS"),sQuery(id+"F0.wireOp",EDGE,"E5.MirrorCS"),sQuery(id+"F0.wireOp",EDGE,"E6.MirrorCS")])]}),"instanceName":"1"});
            transform(context, id + "F11", {"entities" : qUnion([Q0]), "transformType" : TransformType.TRANSLATION_3D, "dx" : 0 * mm, "dy" : 0 * mm, "dz" : -20 * mm, "makeCopy" : false});
        }
        {
            var Q0;
            Q0=qCreatedBy(makeId("Right.planeOp"),FACE);
            var sketch = newSketch(context, id + "F12", { "sketchPlane" : qUnion([Q0])});
            skCircle(sketch, "E12.0.0", {"center": v(20.98, 30) * mm, "radius": 6.5 * mm});
            skLineSegment(sketch, "E13.bottom", {"start": v(31.8, 38.57) * mm, "end": v(6.18, 38.57) * mm});
            skLineSegment(sketch, "E13.top", {"start": v(31.8, 40.39) * mm, "end": v(6.18, 40.39) * mm});
            skLineSegment(sketch, "E13.left", {"start": v(31.8, 38.57) * mm, "end": v(31.8, 40.39) * mm});
            skLineSegment(sketch, "E13.right", {"start": v(6.18, 38.57) * mm, "end": v(6.18, 40.39) * mm});
            skSolve(sketch);
        }
        {
            var Q0;
            Q0=makeQuery(id+"F12.imprint","IMPRINT",FACE,{"disambiguationData":[TD([[makeQuery(id+"F12.imprint","IMPRINT",EDGE,{"derivedFrom":sQuery(id+"F12.wireOp",EDGE,"E13.bottom")}),-1.0]])]});
            extrude(context, id + "F13", {"entities" : qUnion([Q0]), "operationType" : NewBodyOperationType.REMOVE, "endBound" : BoundingType.THROUGH_ALL, "oppositeDirection" : true, "depth" : 25 * mm});
        }
        {
            var Q0;
            Q0=makeQuery(id+"F1.opRevolve","SWEPT_BODY",BODY,{"disambiguationData":[OSD([sQuery(id+"F0.wireOp",EDGE,"E0.bottom"),sQuery(id+"F0.wireOp",EDGE,"E0.top"),sQuery(id+"F0.wireOp",EDGE,"E0.left"),sQuery(id+"F0.wireOp",EDGE,"E0.right"),sQuery(id+"F0.wireOp",EDGE,"E1.bottom"),sQuery(id+"F0.wireOp",EDGE,"E1.top"),sQuery(id+"F0.wireOp",EDGE,"E1.right"),sQuery(id+"F0.wireOp",EDGE,"E3.MirrorCS"),sQuery(id+"F0.wireOp",EDGE,"E5.MirrorCS"),sQuery(id+"F0.wireOp",EDGE,"E6.MirrorCS")])]});
            transform(context, id + "F14", {"entities" : qUnion([Q0]), "transformType" : TransformType.TRANSLATION_3D, "dx" : 0 * mm, "dy" : 0 * mm, "dz" : -40 * mm, "makeCopy" : true});
        }
    });
